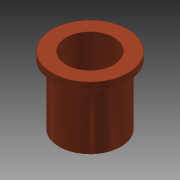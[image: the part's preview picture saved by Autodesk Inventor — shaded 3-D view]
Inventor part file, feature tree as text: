
AUTODESK INVENTOR PART (.ipt)
format: ipt  version: 2015 (Build 190159000, 159)  size: 91,136 bytes
history: native  units: in
note: dims shown in document units (in); Inventor stores cm internally (conversion verified against a paired STEP export)
features: revolve x1, sketch x1
ambient origin geometry x8: Origin, YZ Plane, XZ Plane, XY Plane, X Axis, Y Axis, Z Axis, Center Point
bodies: Solid1 (feature_tree)
feature tree (2):
  revolve  "Revolution1"  [1 undecoded]
  sketch  "Sketch1"  dims[d0=90.0deg d1=0.3937in d3=0.5118in d4=0.0591in d5=0.6299in]
note: 1 required parameter value undecoded (feature->parameter linkage not recoverable at this tier; creation-order binding heuristic only, values carry confidence <= 0.55)
